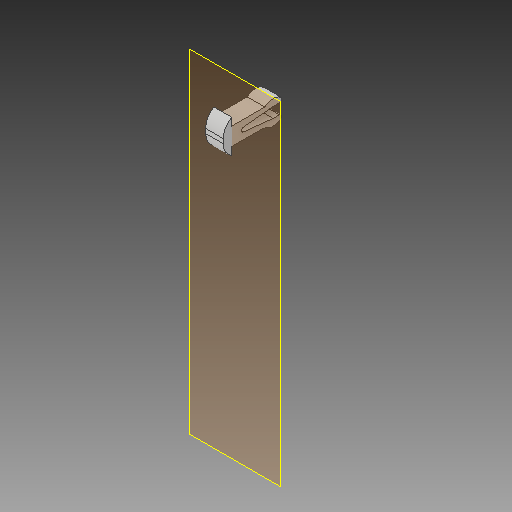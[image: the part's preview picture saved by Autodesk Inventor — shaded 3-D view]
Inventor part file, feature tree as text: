
AUTODESK INVENTOR PART (.ipt)
format: ipt  version: 2017 (Build 210142000, 142)  size: 149,504 bytes
history: native  units: mm
features: extrude x4, sketch x4, other x4, reference x3, fillet x2, plane x1
ambient origin geometry x8: Origin, YZ Plane, XZ Plane, XY Plane, X Axis, Y Axis, Z Axis, Center Point
bodies: Solid1 (feature_tree)
feature tree (18):
  plane  "Work Plane1"
  extrude  "Extrusion1"  Depth=12.0mm TaperAngle=0.0deg
  extrude  "Extrusion2"  Depth=2.0mm TaperAngle=0.0deg
  fillet  "Fillet1"  Radius=4.0mm
  extrude  "Extrusion3"  Depth=3.0mm
  extrude  "Extrusion4"  Depth=4.0mm
  fillet  "Fillet2"  Radius=2.5mm
  sketch  "Sketch1"  dims[d0=45.0deg d1=12.0mm d2=0.0mm]
  reference  "Reference1"
  sketch  "Sketch2"  dims[d3=8.0mm d4=2.0mm d5=0.0mm d6=4.0mm]
  reference  "Reference2"
  sketch  "Sketch3"  dims[d7=3.0mm d8=3.0mm]
  reference  "Reference3"
  sketch  "Sketch4"  dims[d9=2.0mm d10=0.0mm d11=4.0mm d12=2.5mm d13=0.5mm d14=2.0mm d15=0.0mm d16=0.5mm]
  parser-record x1  (decoder bookkeeping rows leaked as tree rows — omitted from the tree; the rows remain in map.json)
  other  "assembly_full.iam"
  other  "top_right:1"
  other  "base:1"
note: 1 file-system path scrubbed to <path> (originals preserved in map.json)
